# Revit family: AFX-Oscar-Flush_mount+
name_source: partatom
category: Lighting Fixtures
units: mm (PartAtom-declared; Revit-internal decimal feet)

## family parameters
Cut with Voids When Loaded = No
Host = Face
Light Source = Yes
Part Type = Normal
Room Calculation Point = No
Round Connector Dimension = Use Diameter
Shared = No

## types (15) — shared parameters
Apparent Load = 0 VA
Assembly Code = D5020200
Body Finish = AFX - Satin Nickel
Color Filter = 16777215
Color Rendering Index = 90
Default Elevation = 48"
Depth = 2 1/2"
Dimming Lamp Color Temperature Shift = <None>
Emit Shape Visible in Rendering = No
Lamp = LED
Manufacturer = AFX Inc
Product Documentation Link = https://www.afxinc.com
Revit Model Built By = https://servex-us.com
Screen Finish = AFX - Diffuser
Tilt Angle = 90.00°
Type Comments = COLE
URL = https://www.afxinc.com
Voltage = 120 V
Wattage Comments = 19W

## per-type parameters (varying)
| type | Description | Diameter | Emit from Circle Diameter | Photometric Web File | Rad |
| OSCF11-2700 | 11'' Flush Mount, 2700K | 11" | 11" | OSCF - 11OSCF11LAJD1xx_2700K_IES.IES | 5 1/2" |
| OSCF14-2700 | 14'' Flush Mount, 2700K | 14" | 14" | OSCF - 14OSCF14LAJD1xx_2700K_IES.IES | 7" |
| OSCF19-2700 | 19'' Flush Mount, 2700K | 19" | 19" | OSCF - 19OSCF19LAJD1xx_2700K_IES.IES | 9 1/2" |
| OSCF11-3000 | 11'' Flush Mount, 3000K | 11" | 11" | OSCF - 11OSCF11LAJD1xx_3000K_IES.IES | 5 1/2" |
| OSCF11-3500 | 11'' Flush Mount, 3500K | 11" | 11" | OSCF - 11OSCF11LAJD1xx_3500K_IES.IES | 5 1/2" |
| OSCF11-4000 | 11'' Flush Mount, 4000K | 11" | 11" | OSCF - 11OSCF11LAJD1xx_4000K_IES.IES | 5 1/2" |
| OSCF11-5000 | 11'' Flush Mount, 5000K | 11" | 11" | OSCF - 11OSCF11LAJD1xx_5000K_IES.IES | 5 1/2" |
| OSCF14-3000 | 14'' Flush Mount, 3000K | 14" | 14" | OSCF - 14OSCF14LAJD1xx_3000K_IES.IES | 7" |
| OSCF14-3500 | 14'' Flush Mount, 3500K | 14" | 14" | OSCF - 14OSCF14LAJD1xx_3500K_IES.IES | 7" |
| OSCF14-4000 | 14'' Flush Mount, 4000K | 14" | 14" | OSCF - 14OSCF14LAJD1xx_4000K_IES.IES | 7" |
| OSCF14-5000 | 14'' Flush Mount, 5000K | 14" | 14" | OSCF - 14OSCF14LAJD1xx_5000K_IES.IES | 7" |
| OSCF19-3000 | 19'' Flush Mount, 3000K | 19" | 19" | OSCF - 19OSCF19LAJD1xx_3000K_IES.IES | 9 1/2" |
| OSCF19-3500 | 19'' Flush Mount, 3500K | 19" | 19" | OSCF - 19OSCF19LAJD1xx_3000K_IES.IES | 9 1/2" |
| OSCF19-4000 | 19'' Flush Mount, 4000K | 19" | 19" | OSCF - 19OSCF19LAJD1xx_4000K_IES.IES | 9 1/2" |
| OSCF19-5000 | 19'' Flush Mount, 5000K | 19" | 19" | OSCF - 19OSCF19LAJD1xx_5000K_IES.IES | 9 1/2" |

note: column(s) folded — value = type name in every type: Model

## geometry (parser evidence)
native form markers: Sweep x3
no freeform markers — native parametric forms only
